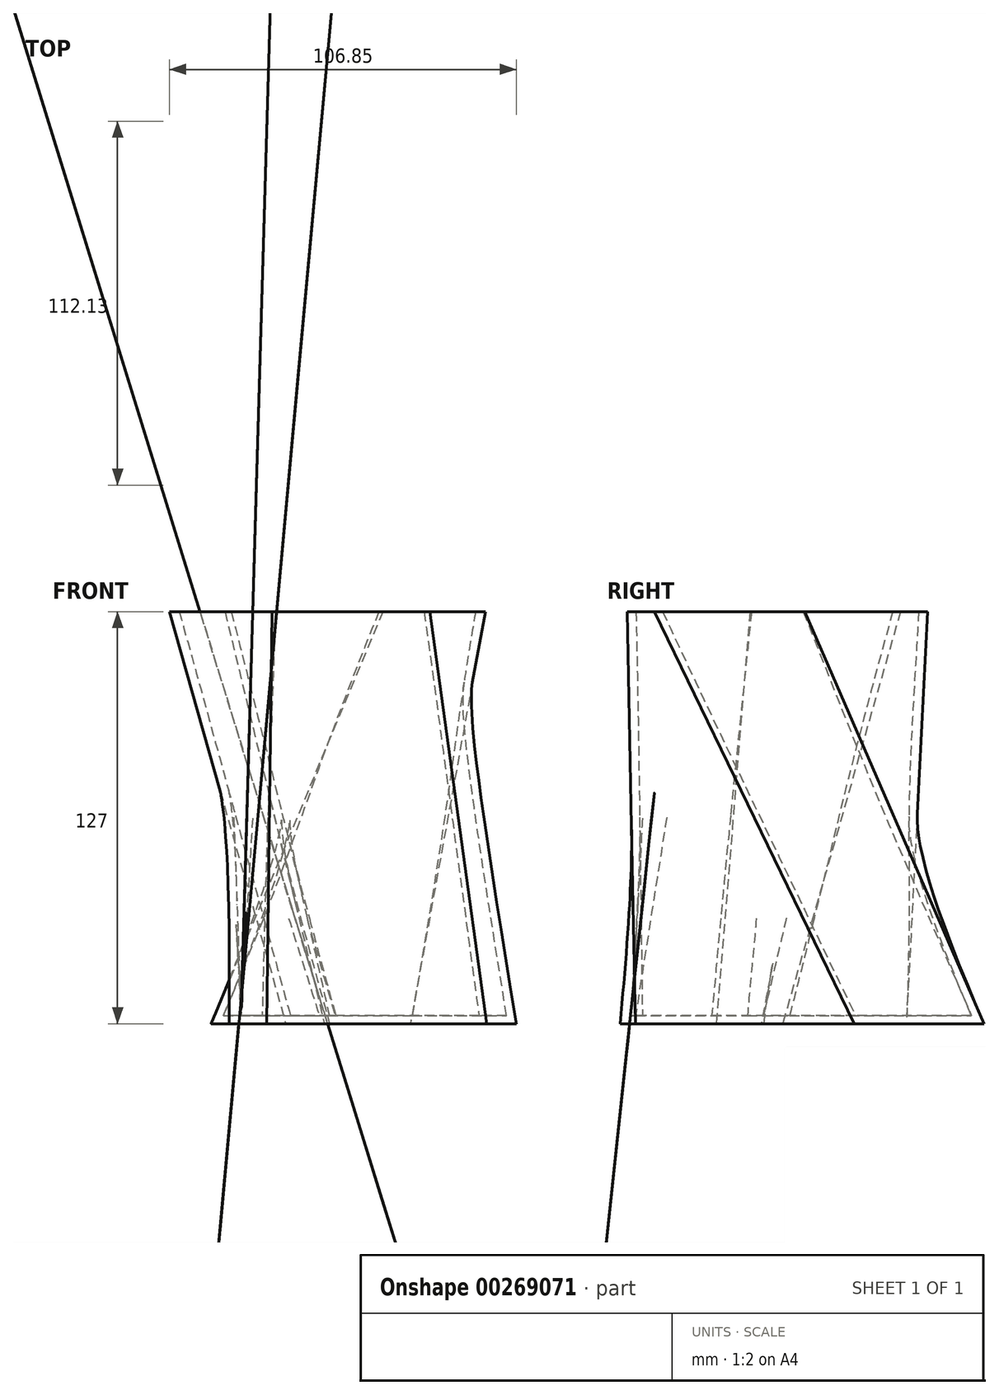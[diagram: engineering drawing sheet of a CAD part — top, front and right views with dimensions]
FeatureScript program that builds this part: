
annotation { "Feature Type Name" : "Feature", "Feature Type Description" : "" }
export const myFeature = defineFeature(function(context is Context, id is Id, definition is map)
    precondition{}
    {
        {
            var Q0;
            Q0=qCreatedBy(makeId("Top.planeOp"),FACE);
            var sketch = newSketch(context, id + "F0", { "sketchPlane" : qUnion([Q0])});
            skFitSpline(sketch, "E0", {"points": [v(0, 0) * mm, v(-35.2, 43.23) * mm, v(57.61, 50.8) * mm, v(-30.02, -47.99) * mm, v(0, -4.17) * mm, v(0, -4.97) * mm, v(0, 0) * mm]});
            skSolve(sketch);
        }
        {
            var Q0;
            Q0=qCreatedBy(makeId("Top.planeOp"),FACE);
            cPlane(context, id + "F1", {"entities" : qUnion([Q0]), "cplaneType" : CPlaneType.OFFSET, "offset" : 127 * mm, "width" : 152.4 * mm, "height" : 152.4 * mm});
        }
        {
            var Q0;
            Q0=qCreatedBy(id+"F1.planeOp",FACE);
            var sketch = newSketch(context, id + "F2", { "sketchPlane" : qUnion([Q0])});
            skCircle(sketch, "E1.cCircle", {"center": v(0, 0) * mm, "radius": 49.37 * mm, "construction": true});
            skLineSegment(sketch, "E1.0", {"start": v(-17.04, -46.34) * mm, "end": v(-48.65, -8.41) * mm});
            skLineSegment(sketch, "E1.1", {"start": v(-48.65, -8.41) * mm, "end": v(-31.6, 37.93) * mm});
            skLineSegment(sketch, "E1.2", {"start": v(-31.6, 37.93) * mm, "end": v(17.04, 46.34) * mm});
            skLineSegment(sketch, "E1.3", {"start": v(17.04, 46.34) * mm, "end": v(48.65, 8.41) * mm});
            skLineSegment(sketch, "E1.4", {"start": v(48.65, 8.41) * mm, "end": v(31.6, -37.93) * mm});
            skLineSegment(sketch, "E1.5", {"start": v(31.6, -37.93) * mm, "end": v(-17.04, -46.34) * mm});
            skSolve(sketch);
        }
        {
            var Q0;
            Q0=makeQuery(id+"F2.imprint","IMPRINT",FACE,{"disambiguationData":[TD([[makeQuery(id+"F2.imprint","IMPRINT",EDGE,{"derivedFrom":sQuery(id+"F2.wireOp",EDGE,"E1.0")}),-1.0]])]});
            var Q1;
            Q1=makeQuery(id+"F0.imprint","IMPRINT",FACE,{"disambiguationData":[TD([[makeQuery(id+"F0.imprint","IMPRINT",EDGE,{"derivedFrom":sQuery(id+"F0.wireOp",EDGE,"E0")}),-1.0]])]});
            loft(context, id + "F3", {"sheetProfilesArray" : [{ "sheetProfileEntities" : qUnion([Q0]) }, { "sheetProfileEntities" : qUnion([Q1]) }]});
        }
        {
            var Q0;
            Q0=makeQuery(id+"F3.opLoft","CAP_FACE",FACE,{"disambiguationData":[OSD([makeQuery(id+"F2.imprint","IMPRINT",FACE,{"disambiguationData":[TD([[makeQuery(id+"F2.imprint","IMPRINT",EDGE,{"derivedFrom":sQuery(id+"F2.wireOp",EDGE,"E1.0")}),-1.0]])]})])],"isStart":true});
            shell(context, id + "F4", {"entities" : qUnion([Q0]), "thickness" : 2.54 * mm});
        }
    });
